# Revit family: BuzziPleat - Suspended
name_source: partatom
category: Lighting Fixtures
revit_build: Autodesk Revit 2018 (Build: 20190510_1515(x64)
units: mm (PartAtom-declared; Revit-internal decimal feet)

## family parameters
Always vertical = Yes
Cut with Voids When Loaded = No
Host = Ceiling
Light Source = Yes
OmniClass Number = 23.80.70.11
OmniClass Title = Luminaries for Internal Lighting
Part Type = Normal
Room Calculation Point = No
Round Connector Dimension = Use Diameter
Shared = No

## types (8) — shared parameters
BuzziPleat Ripple Shade = <By Category>
Color Filter = 16777215
Dimming Lamp Color Temperature Shift = <None>
Drop From Ceiling = 3' - 0"
Globe Material = <By Category>
Lens = <By Category>
Light Source Symbol Size = 2' - 0"

## per-type parameters (varying)
| type | BuzziPleat Edel 100cm | BuzziPleat Edel 150cm | BuzziPleat Ripple 100cm | BuzziPleat Ripple 150cm | Globe | Spot | Wires |
| BuzziPleat Edel 150cm - Spot | No | Yes | No | No | No | Yes | <By Category> |
| BuzziPleat Edel 100cm - Spot | Yes | No | No | No | No | Yes | Default |
| BuzziPleat Ripple 100cm - Spot | No | No | Yes | No | No | Yes | <By Category> |
| BuzziPleat Ripple 150cm - Spot | No | No | No | Yes | No | Yes | <By Category> |
| BuzziPleat Ripple 150cm - Globe | No | No | No | Yes | Yes | No | <By Category> |
| BuzziPleat Ripple 100cm - Globe | No | No | Yes | No | Yes | No | <By Category> |
| BuzziPleat Edel 150cm - Globe | No | Yes | No | No | Yes | No | <By Category> |
| BuzziPleat Edel 100cm - Globe | Yes | No | No | No | Yes | No | Default |

## geometry (parser evidence)
native form markers: Sweep x6
no freeform markers — native parametric forms only
